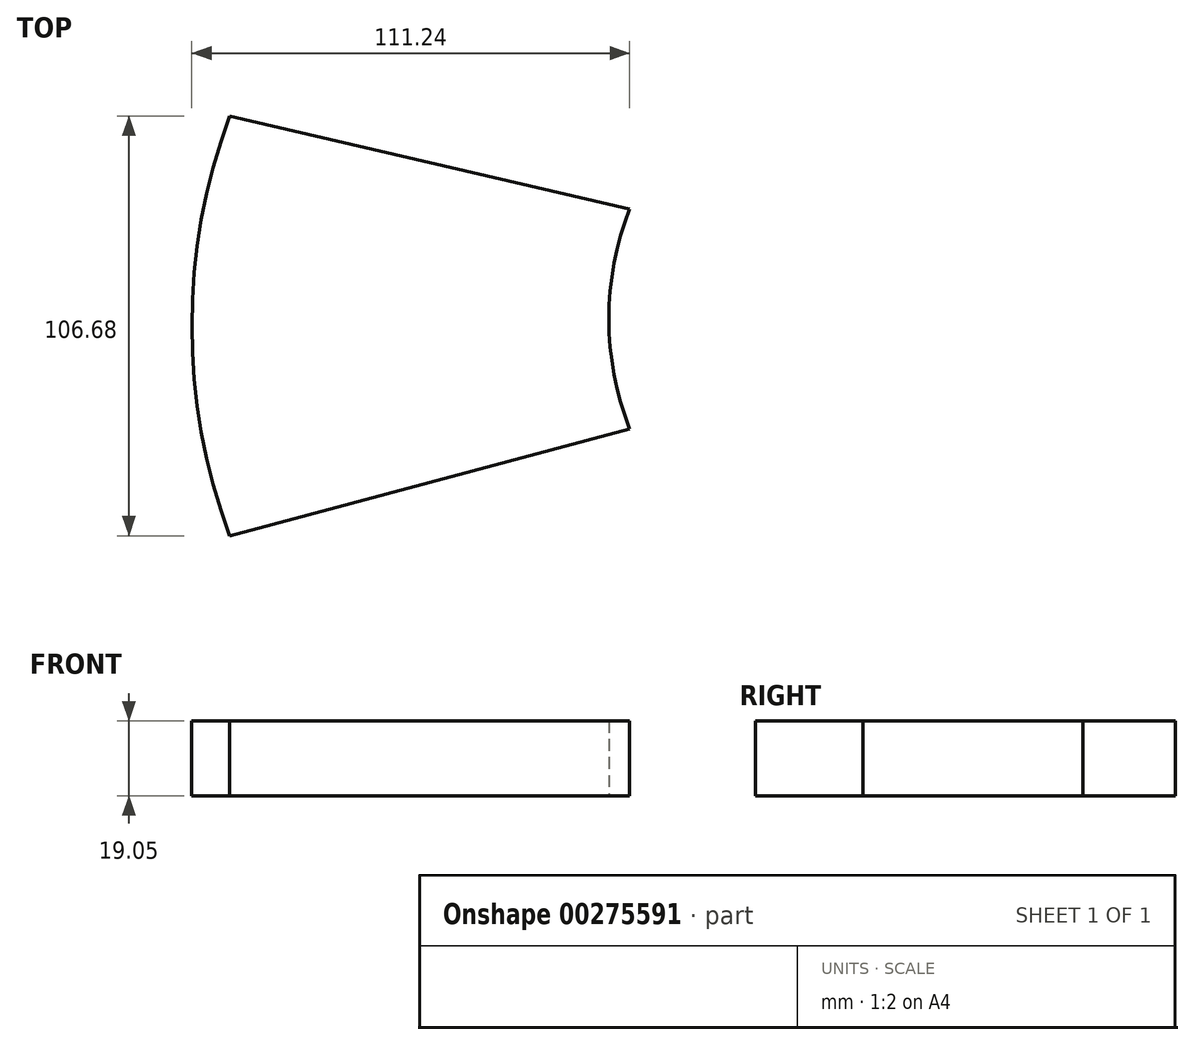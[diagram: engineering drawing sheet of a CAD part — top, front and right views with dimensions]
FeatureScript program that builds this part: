
annotation { "Feature Type Name" : "Feature", "Feature Type Description" : "" }
export const myFeature = defineFeature(function(context is Context, id is Id, definition is map)
    precondition{}
    {
        {
            var Q0;
            Q0=qCreatedBy(makeId("Top.planeOp"),FACE);
            var sketch = newSketch(context, id + "F0", { "sketchPlane" : qUnion([Q0])});
            skLineSegment(sketch, "E0", {"start": v(-57.26, 0) * mm, "end": v(44.34, 0) * mm});
            skLineSegment(sketch, "E1", {"start": v(-57.26, 0) * mm, "end": v(-57.26, -27.21) * mm});
            skLineSegment(sketch, "E2", {"start": v(-57.26, -27.21) * mm, "end": v(-57.26, 79.47) * mm});
            skLineSegment(sketch, "E3", {"start": v(44.34, 0) * mm, "end": v(44.34, 55.88) * mm});
            skLineSegment(sketch, "E4", {"start": v(-57.26, 79.47) * mm, "end": v(44.34, 55.88) * mm});
            skLineSegment(sketch, "E5", {"start": v(44.34, 0) * mm, "end": v(-57.26, -27.21) * mm});
            skArc(sketch, "E6", {"start": v(-57.26, 79.47) * mm, "mid": v(-66.9, 26.13) * mm, "end": v(-57.26, -27.21) * mm});
            skArc(sketch, "E7", {"start": v(44.34, 55.88) * mm, "mid": v(39.03, 27.94) * mm, "end": v(44.34, 0) * mm});
            skSolve(sketch);
        }
        {
            var Q0;
            {var subQ0=sQuery(id+"F0.wireOp",EDGE,"E0");Q0=makeQuery(id+"F0.imprint","IMPRINT",FACE,{"disambiguationData":[TD([[makeQuery(id+"F0.imprint","IMPRINT",EDGE,{"derivedFrom":subQ0}),1.0]])]});}
            var Q1;
            {var subQ0=sQuery(id+"F0.wireOp",EDGE,"E0");Q1=makeQuery(id+"F0.imprint","IMPRINT",FACE,{"disambiguationData":[TD([[makeQuery(id+"F0.imprint","IMPRINT",EDGE,{"derivedFrom":subQ0}),-1.0]])]});}
            var Q2;
            {var subQ2=sQuery(id+"F0.wireOp",EDGE,"E6");Q2=makeQuery(id+"F0.imprint","IMPRINT",FACE,{"disambiguationData":[TD([[makeQuery(id+"F0.imprint","IMPRINT",EDGE,{"derivedFrom":subQ2}),1.0]])]});}
            extrude(context, id + "F1", {"entities" : qUnion([Q0, Q1, Q2]), "depth" : 19.05 * mm});
        }
    });
